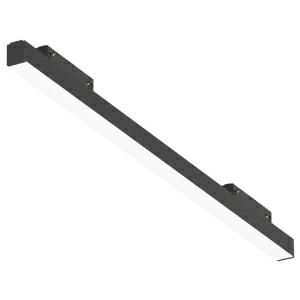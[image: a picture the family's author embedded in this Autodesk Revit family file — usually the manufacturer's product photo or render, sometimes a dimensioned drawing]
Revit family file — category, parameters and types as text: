
# Revit family: 2look4_25_magtrack_ledline_l_620mm_led_48v_2700k_7w_cri80_810-0160_e44e
name_source: partatom
category: Leuchten
revit_build: Autodesk Revit 2016 (Build: 20190508_0715(x64)
units: mm (PartAtom-declared; Revit-internal decimal feet)

## family parameters
Basisbauteil = Fläche
Beim Laden mit Abzugskörper schneiden = Nein
Bemaßung runder Anschluss = Durchmesser verwenden
Gemeinsam genutzt = Nein
Lichtquelle = Nein
Raumberechnungspunkt = Nein
Teiletyp = Normal

## types (1)
- 810-0160 (6 x LED, 100 lm, 1.1 W, 2700K)
    Beschreibung = The insert consists of aluminum-die-cast. The ballast is integrated and allows for an operation with 48V. 2LOOK4 25 MAGTRACK / HYPRO 30 (# 810-0160) ist not dimmable (on/off).
    CIE Flux Codes = 56 84 97 99 60
    Color Rendering = 1A/90…99
    Color Temperature = 2700K
    Height = 0 mm  [stored 0 ft]
    Hersteller = Prolicht
    Lamp Light Flux = 100 lm
    Lamp Power = 1.1 W
    Lamp count = 6
    Lampe = 6 x LED
    Length = 620 mm
    Luminous efficacy = 54 lm/W
    ModVariant = Nein
    Modell = 810-0160
    Mounting Place = Ceiling
    Mounting Type = Recessed
    Number of Poles = 1
    OnlyDefault = Ja
    Power Factor = 1
    Product Name = 2LOOK4 25 MAGTRACK__LEDLINE L=620mm LED 48V 2700K 7W CRI80
    Product group = Trimless recessed profile systems
    ProductGroupID = 414
    Protection Class = Protection class
    Protection Degree = Degree of protection
    RLX_Detail_Level = 1
    RlxData = <blob elided: 276237 chars, md5=e19a6a03>
    Scheinlast = 7 VA
    Socket = socket
    Standby Power = 0 W
    System Light Flux = 358 lm
    System Power = 7 W
    Typenbild = 810-0160.jpg
    Typenkommentare = The insert consists of aluminum-die-cast. The ballast is integrated and allows for an operation with 48V. 2LOOK4 25 MAGTRACK / HYPRO 30 (# 810-0160) ist not dimmable (on/off).
    URL = http://relux.com
    VarID = 810-0160
    Voltage = 0 V
    Vorgabe-Ansicht = 1800 mm
    Weight = 0.00 kg
    Width = 23 mm

note: [stored X ft] marks values corroborated as IEEE doubles in the binary element streams (Revit-internal decimal feet)

## geometry (parser evidence)
native form markers: Sweep x8
no freeform markers — native parametric forms only
